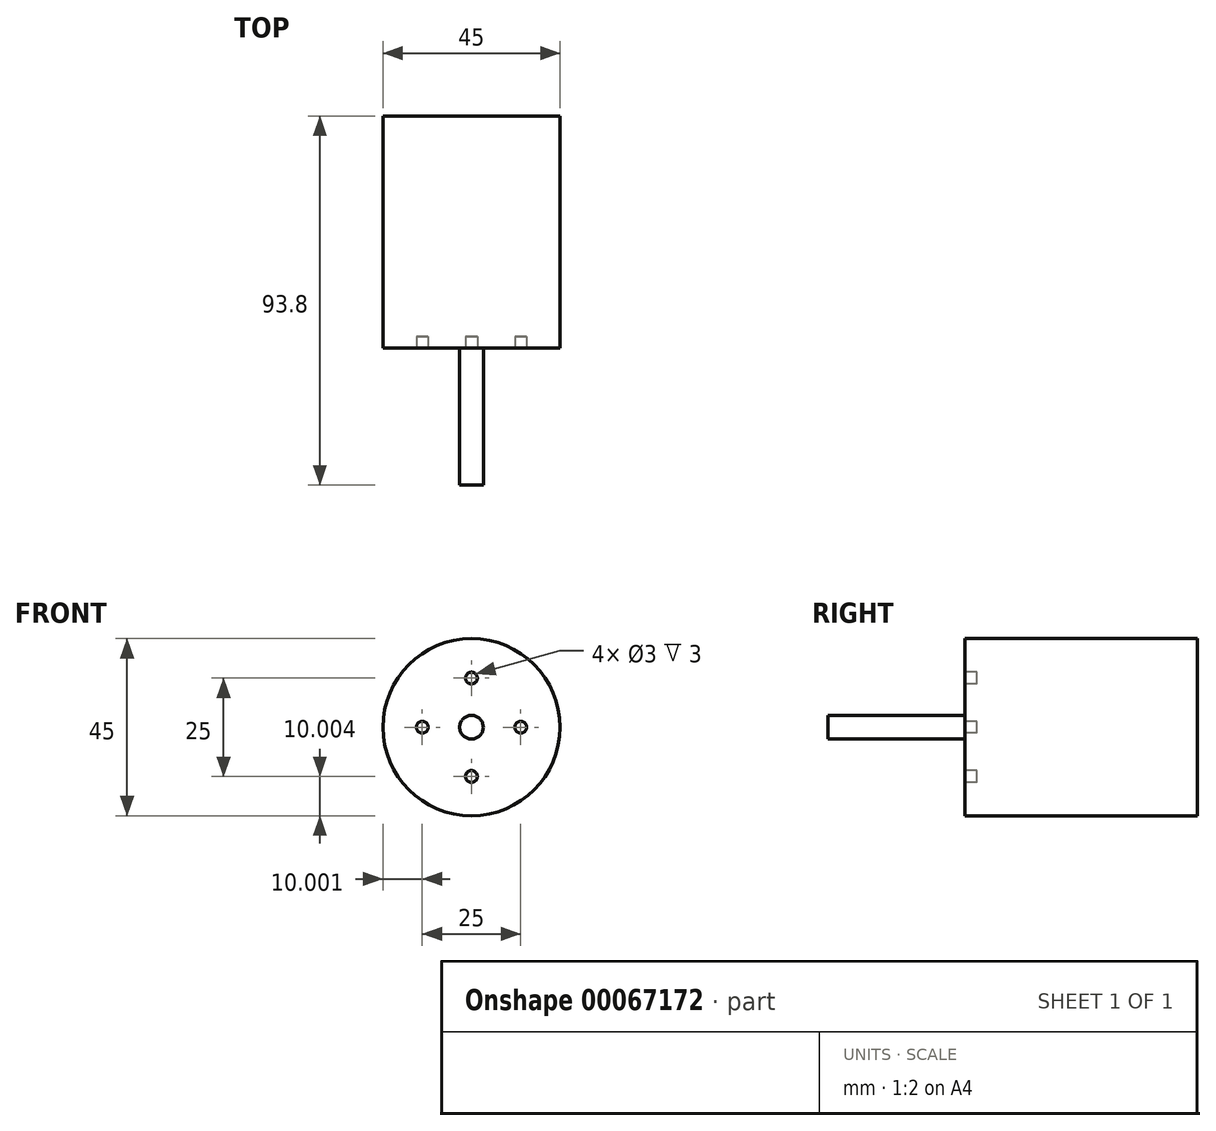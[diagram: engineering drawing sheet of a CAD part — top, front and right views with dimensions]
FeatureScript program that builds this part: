
annotation { "Feature Type Name" : "Feature", "Feature Type Description" : "" }
export const myFeature = defineFeature(function(context is Context, id is Id, definition is map)
    precondition{}
    {
        {
            var Q0;
            Q0=qCreatedBy(makeId("Front.planeOp"),FACE);
            var sketch = newSketch(context, id + "F0", { "sketchPlane" : qUnion([Q0])});
            skCircle(sketch, "E0", {"center": v(-27.66, 18.85) * mm, "radius": 22.5 * mm});
            skCircle(sketch, "E1", {"center": v(-27.66, 18.85) * mm, "radius": 3 * mm});
            skLineSegment(sketch, "E2", {"start": v(-27.66, 31.89) * mm, "end": v(-27.66, 1.21) * mm, "construction": true});
            skLineSegment(sketch, "E3", {"start": v(-42.12, 18.85) * mm, "end": v(-9.6, 18.85) * mm, "construction": true});
            skCircle(sketch, "E4", {"center": v(-40.16, 18.85) * mm, "radius": 1.5 * mm, "construction": true});
            skCircle(sketch, "E5", {"center": v(-27.66, 31.35) * mm, "radius": 1.5 * mm, "construction": true});
            skCircle(sketch, "E6", {"center": v(-15.16, 18.85) * mm, "radius": 1.5 * mm, "construction": true});
            skCircle(sketch, "E7", {"center": v(-27.66, 6.35) * mm, "radius": 1.5 * mm, "construction": true});
            skSolve(sketch);
        }
        {
            var Q0;
            Q0=makeQuery(id+"F0.imprint","IMPRINT",FACE,{"disambiguationData":[TD([[makeQuery(id+"F0.imprint","IMPRINT",EDGE,{"derivedFrom":sQuery(id+"F0.wireOp",EDGE,"E0")}),1.0]])]});
            extrude(context, id + "F1", {"entities" : qUnion([Q0]), "depth" : 59 * mm});
        }
        {
            var Q0;
            Q0=makeQuery(id+"F0.imprint","IMPRINT",FACE,{"disambiguationData":[TD([[makeQuery(id+"F0.imprint","IMPRINT",EDGE,{"derivedFrom":sQuery(id+"F0.wireOp",EDGE,"E1")}),1.0]])]});
            extrude(context, id + "F2", {"entities" : qUnion([Q0]), "operationType" : NewBodyOperationType.ADD, "depth" : 93.8 * mm});
        }
        {
            var Q0;
            Q0=makeQuery(id+"F1.opExtrude","CAP_FACE",FACE,{"disambiguationData":[OSD([sQuery(id+"F0.wireOp",EDGE,"E0"),sQuery(id+"F0.wireOp",EDGE,"E1")])],"isStart":false});
            var sketch = newSketch(context, id + "F3", { "sketchPlane" : qUnion([Q0])});
            skCircle(sketch, "E8.0", {"center": v(-27.66, 31.35) * mm, "radius": 1.5 * mm});
            skCircle(sketch, "E8.1", {"center": v(-40.16, 18.85) * mm, "radius": 1.5 * mm});
            skCircle(sketch, "E8.2", {"center": v(-27.66, 6.35) * mm, "radius": 1.5 * mm});
            skCircle(sketch, "E8.3", {"center": v(-15.16, 18.85) * mm, "radius": 1.5 * mm});
            skSolve(sketch);
        }
        {
            var Q0;
            Q0=qSketchRegion(id+"F3",true);
            extrude(context, id + "F4", {"entities" : qUnion([Q0]), "operationType" : NewBodyOperationType.REMOVE, "oppositeDirection" : true, "depth" : 3 * mm});
        }
    });
